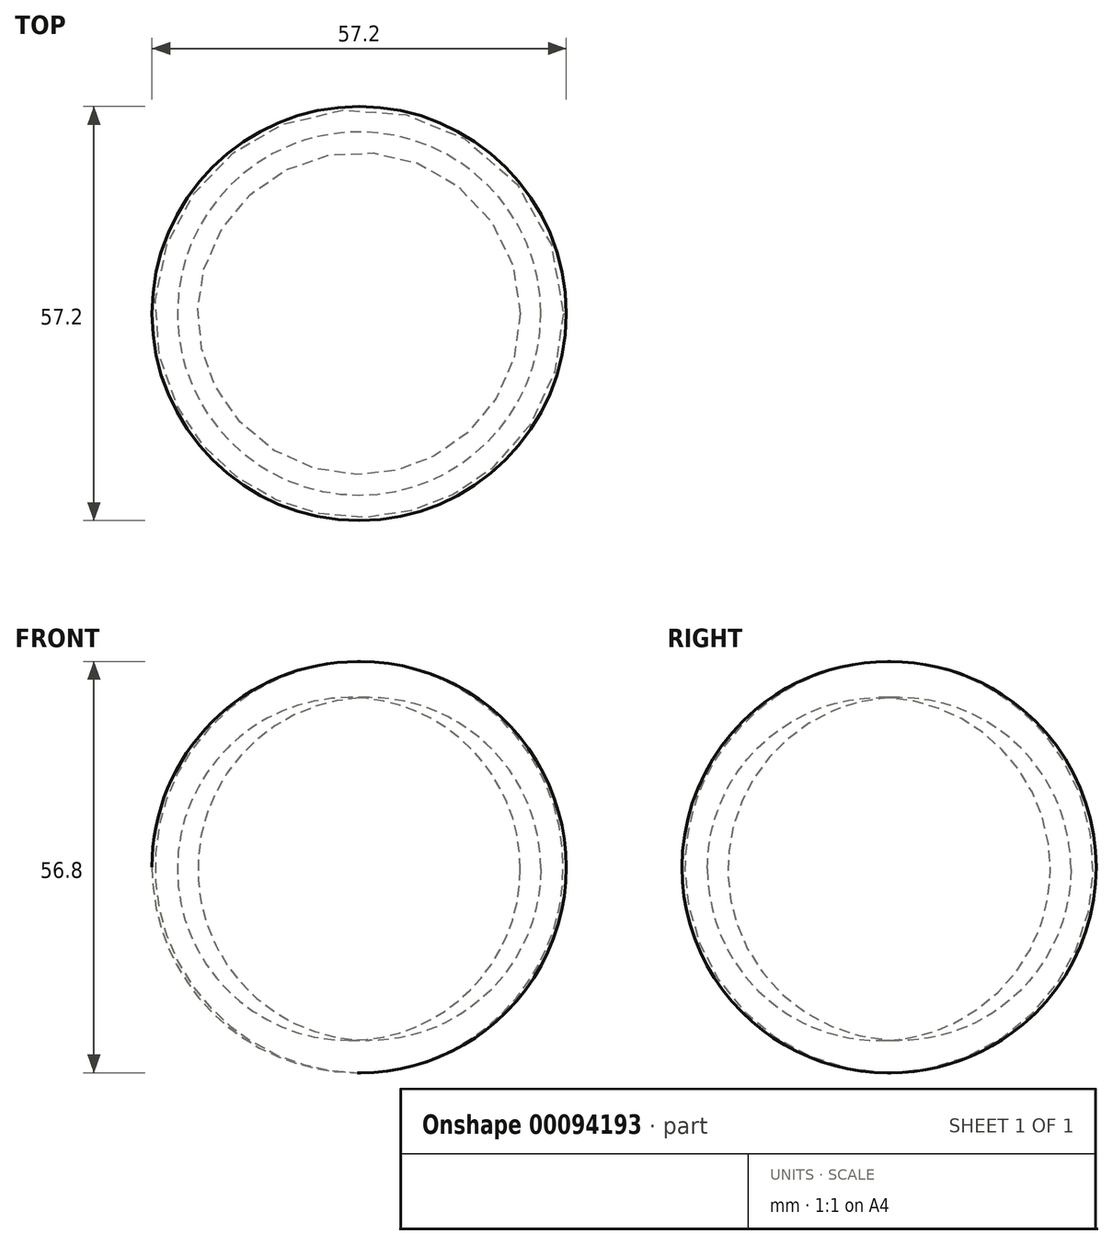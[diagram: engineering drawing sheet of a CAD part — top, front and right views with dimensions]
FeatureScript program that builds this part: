
annotation { "Feature Type Name" : "Feature", "Feature Type Description" : "" }
export const myFeature = defineFeature(function(context is Context, id is Id, definition is map)
    precondition{}
    {
        {
            var Q0;
            Q0=qCreatedBy(makeId("Right.planeOp"),FACE);
            var sketch = newSketch(context, id + "F0", { "sketchPlane" : qUnion([Q0])});
            skArc(sketch, "E0", {"start": v(0, 28) * mm, "mid": v(-28.6, -0.4) * mm, "end": v(0, -28.8) * mm});
            skArc(sketch, "E1", {"start": v(0, 22.98) * mm, "mid": v(-25.1, -0.66) * mm, "end": v(0, -24.3) * mm});
            skLineSegment(sketch, "E2", {"start": v(0, -28.8) * mm, "end": v(0, -24.3) * mm});
            skLineSegment(sketch, "E3", {"start": v(0, 22.98) * mm, "end": v(0, 28) * mm});
            skSolve(sketch);
        }
        {
            var Q0;
            Q0=makeQuery(id+"F0.imprint","IMPRINT",FACE,{"disambiguationData":[TD([[makeQuery(id+"F0.imprint","IMPRINT",EDGE,{"derivedFrom":sQuery(id+"F0.wireOp",EDGE,"E0")}),1.0]])]});
            var Q1;
            Q1=sQuery(id+"F0.wireOp",EDGE,"E2");
            revolve(context, id + "F1", {"entities" : qUnion([Q0]), "axis" : qUnion([Q1]), "revolveType" : RevolveType.FULL});
        }
    });
